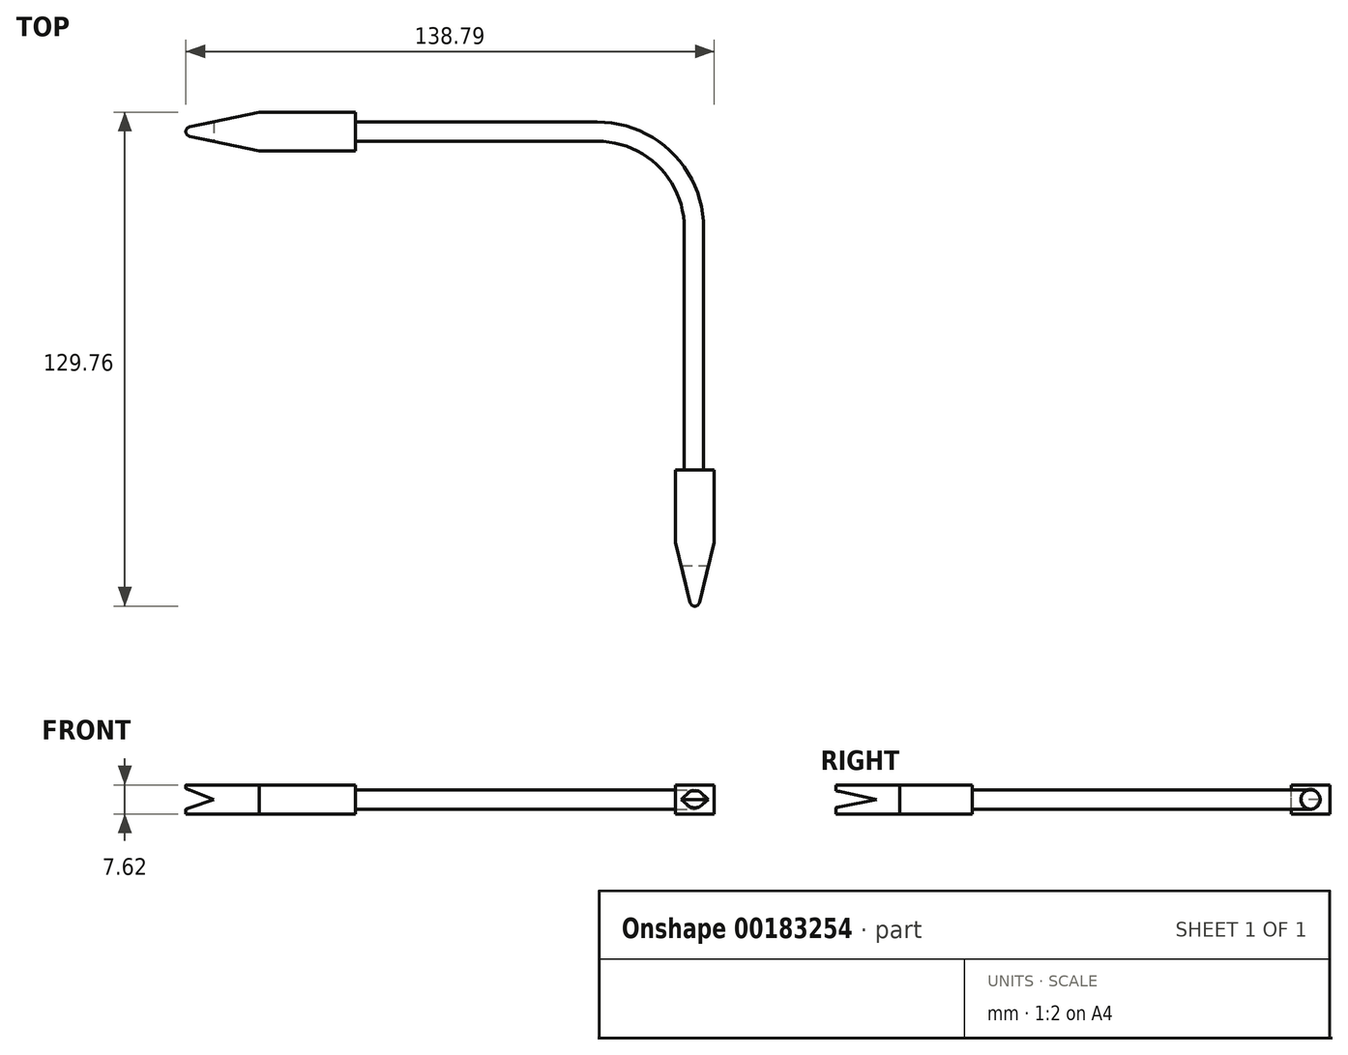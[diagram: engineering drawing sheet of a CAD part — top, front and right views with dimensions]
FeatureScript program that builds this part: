
annotation { "Feature Type Name" : "Feature", "Feature Type Description" : "" }
export const myFeature = defineFeature(function(context is Context, id is Id, definition is map)
    precondition{}
    {
        {
            var Q0;
            Q0=qCreatedBy(makeId("Right.planeOp"),FACE);
            var sketch = newSketch(context, id + "F0", { "sketchPlane" : qUnion([Q0])});
            skCircle(sketch, "E0", {"center": v(0, 0) * mm, "radius": 2.54 * mm});
            skSolve(sketch);
        }
        {
            var Q0;
            Q0=qCreatedBy(makeId("Top.planeOp"),FACE);
            var sketch = newSketch(context, id + "F1", { "sketchPlane" : qUnion([Q0])});
            skLineSegment(sketch, "E1", {"start": v(0, 0) * mm, "end": v(63.5, 0) * mm});
            skLineSegment(sketch, "E2", {"start": v(63.5, 0) * mm, "end": v(63.5, -64.55) * mm, "construction": true});
            skArc(sketch, "E3", {"start": v(88.9, -25.4) * mm, "mid": v(81.46, -7.44) * mm, "end": v(63.5, 0) * mm});
            skLineSegment(sketch, "E4", {"start": v(88.9, -25.4) * mm, "end": v(88.9, -88.9) * mm});
            skSolve(sketch);
        }
        {
            var Q0;
            Q0=makeQuery(id+"F0.imprint","IMPRINT",FACE,{"disambiguationData":[TD([[makeQuery(id+"F0.imprint","IMPRINT",EDGE,{"derivedFrom":sQuery(id+"F0.wireOp",EDGE,"E0")}),1.0]])]});
            var Q1;
            Q1=sQuery(id+"F1.wireOp",EDGE,"E1");
            var Q2;
            Q2=sQuery(id+"F1.wireOp",EDGE,"E3");
            var Q3;
            Q3=sQuery(id+"F1.wireOp",EDGE,"E4");
            sweep(context, id + "F2", {"profiles" : qUnion([Q0]), "path" : qUnion([Q1, Q2, Q3])});
        }
        {
            var Q0;
            Q0=qCreatedBy(makeId("Top.planeOp"),FACE);
            var sketch = newSketch(context, id + "F3", { "sketchPlane" : qUnion([Q0])});
            skLineSegment(sketch, "E5.bottom", {"start": v(0, 5.08) * mm, "end": v(-25.36, 5.08) * mm});
            skLineSegment(sketch, "E5.top", {"start": v(0, -5.08) * mm, "end": v(-25.36, -5.08) * mm});
            skLineSegment(sketch, "E5.left", {"start": v(0, 5.08) * mm, "end": v(0, -5.08) * mm});
            skLineSegment(sketch, "E5.right", {"start": v(-25.36, 5.08) * mm, "end": v(-25.36, -5.08) * mm});
            skSolve(sketch);
        }
        {
            var Q0;
            Q0=makeQuery(id+"F3.imprint","IMPRINT",FACE,{"disambiguationData":[TD([[makeQuery(id+"F3.imprint","IMPRINT",EDGE,{"derivedFrom":sQuery(id+"F3.wireOp",EDGE,"E5.bottom")}),1.0]])]});
            extrude(context, id + "F4", {"entities" : qUnion([Q0]), "operationType" : NewBodyOperationType.ADD, "endBound" : BoundingType.SYMMETRIC, "oppositeDirection" : true, "depth" : 7.62 * mm});
        }
        {
            var Q0;
            Q0=makeQuery(id+"F4.opExtrude","CAP_FACE",FACE,{"disambiguationData":[OSD([sQuery(id+"F3.wireOp",EDGE,"E5.bottom"),sQuery(id+"F3.wireOp",EDGE,"E5.top"),sQuery(id+"F3.wireOp",EDGE,"E5.left"),sQuery(id+"F3.wireOp",EDGE,"E5.right")])],"isStart":true});
            var sketch = newSketch(context, id + "F5", { "sketchPlane" : qUnion([Q0])});
            skLineSegment(sketch, "E6", {"start": v(-25.36, 5.08) * mm, "end": v(-49.47, 0) * mm});
            skLineSegment(sketch, "E7", {"start": v(-49.47, 0) * mm, "end": v(-25.36, -5.08) * mm});
            skLineSegment(sketch, "E8", {"start": v(-25.36, -5.08) * mm, "end": v(-25.36, 5.08) * mm});
            skSolve(sketch);
        }
        {
            var Q0;
            Q0=makeQuery(id+"F5.imprint","IMPRINT",FACE,{"disambiguationData":[TD([[makeQuery(id+"F5.imprint","IMPRINT",EDGE,{"derivedFrom":sQuery(id+"F5.wireOp",EDGE,"E6")}),1.0]])]});
            var Q1;
            Q1=makeQuery(id+"F4.opExtrude","CAP_FACE",FACE,{"disambiguationData":[OSD([sQuery(id+"F3.wireOp",EDGE,"E5.bottom"),sQuery(id+"F3.wireOp",EDGE,"E5.top"),sQuery(id+"F3.wireOp",EDGE,"E5.left"),sQuery(id+"F3.wireOp",EDGE,"E5.right")])],"isStart":false});
            extrude(context, id + "F6", {"entities" : qUnion([Q0]), "operationType" : NewBodyOperationType.ADD, "endBound" : BoundingType.UP_TO_SURFACE, "oppositeDirection" : true, "endBoundEntityFace" : qUnion([Q1]), "depth" : 25.4 * mm});
        }
        {
            var Q0;
            Q0=makeQuery(id+"F6.opExtrude","SWEPT_EDGE",EDGE,{"disambiguationData":[OSD([sQuery(id+"F5.wireOp",EDGE,"E6"),sQuery(id+"F5.wireOp",EDGE,"E7")])]});
            fillet(context, id + "F7", {"entities" : qUnion([Q0]), "radius" : 1.27 * mm, "tangentPropagation" : true, "allowEdgeOverflow" : false});
        }
        {
            var Q0;
            Q0=makeQuery(id+"F4.opExtrude","SWEPT_FACE",FACE,{"disambiguationData":[OSD([sQuery(id+"F3.wireOp",EDGE,"E5.top")])]});
            var sketch = newSketch(context, id + "F8", { "sketchPlane" : qUnion([Q0])});
            skLineSegment(sketch, "E9", {"start": v(-37.22, 0) * mm, "end": v(-46.26, 3.53) * mm});
            skLineSegment(sketch, "E10", {"start": v(-37.22, 0) * mm, "end": v(-46.26, -3.1) * mm});
            skLineSegment(sketch, "E11", {"start": v(-46.26, -3.1) * mm, "end": v(-46.26, 3.53) * mm});
            skSolve(sketch);
        }
        {
            var Q0;
            Q0=makeQuery(id+"F8.imprint","IMPRINT",FACE,{"disambiguationData":[TD([[makeQuery(id+"F8.imprint","IMPRINT",EDGE,{"derivedFrom":sQuery(id+"F8.wireOp",EDGE,"E9")}),1.0]])]});
            extrude(context, id + "F9", {"entities" : qUnion([Q0]), "operationType" : NewBodyOperationType.REMOVE, "oppositeDirection" : true, "depth" : 25.4 * mm});
        }
        {
            var Q0;
            Q0=qCreatedBy(makeId("Top.planeOp"),FACE);
            var sketch = newSketch(context, id + "F10", { "sketchPlane" : qUnion([Q0])});
            skLineSegment(sketch, "E12.bottom", {"start": v(84.05, -88.9) * mm, "end": v(94.2, -88.9) * mm, "construction": true});
            skLineSegment(sketch, "E12.left", {"start": v(84.05, -88.9) * mm, "end": v(84.05, -107.95) * mm, "construction": true});
            skLineSegment(sketch, "E12.right", {"start": v(94.2, -88.9) * mm, "end": v(94.2, -107.95) * mm, "construction": true});
            skLineSegment(sketch, "E13.bottom", {"start": v(84.05, -88.9) * mm, "end": v(94.2, -88.9) * mm});
            skLineSegment(sketch, "E13.left", {"start": v(84.05, -88.9) * mm, "end": v(84.05, -107.95) * mm});
            skLineSegment(sketch, "E13.right", {"start": v(94.2, -88.9) * mm, "end": v(94.2, -107.95) * mm});
            skLineSegment(sketch, "E14", {"start": v(84.05, -107.95) * mm, "end": v(89.13, -128.77) * mm});
            skPoint(sketch, "E14.endSnap0", {"position": v(89.13, -107.95) * mm});
            skLineSegment(sketch, "E15", {"start": v(89.13, -128.77) * mm, "end": v(94.2, -107.95) * mm});
            skSolve(sketch);
        }
        {
            var Q0;
            Q0=makeQuery(id+"F10.imprint","IMPRINT",FACE,{"disambiguationData":[TD([[makeQuery(id+"F10.imprint","IMPRINT",EDGE,{"derivedFrom":sQuery(id+"F10.wireOp",EDGE,"E13.bottom")}),-1.0]])]});
            extrude(context, id + "F11", {"entities" : qUnion([Q0]), "operationType" : NewBodyOperationType.ADD, "endBound" : BoundingType.SYMMETRIC, "oppositeDirection" : true, "depth" : 7.62 * mm});
        }
        {
            var Q0;
            Q0=makeQuery(id+"F11.opExtrude","SWEPT_EDGE",EDGE,{"disambiguationData":[OSD([sQuery(id+"F10.wireOp",EDGE,"E14"),sQuery(id+"F10.wireOp",EDGE,"E15")])]});
            fillet(context, id + "F12", {"entities" : qUnion([Q0]), "radius" : 1.27 * mm, "tangentPropagation" : true, "allowEdgeOverflow" : false});
        }
        {
            var Q0;
            Q0=makeQuery(id+"F11.opExtrude","SWEPT_FACE",FACE,{"disambiguationData":[OSD([sQuery(id+"F10.wireOp",EDGE,"E13.right")])]});
            var sketch = newSketch(context, id + "F13", { "sketchPlane" : qUnion([Q0])});
            skLineSegment(sketch, "E16", {"start": v(-114.07, 0) * mm, "end": v(-128.7, 3.18) * mm});
            skLineSegment(sketch, "E17", {"start": v(-114.07, 0) * mm, "end": v(-128.7, -2.94) * mm});
            skLineSegment(sketch, "E18", {"start": v(-128.7, -2.94) * mm, "end": v(-128.7, 3.18) * mm});
            skSolve(sketch);
        }
        {
            var Q0;
            Q0=makeQuery(id+"F13.imprint","IMPRINT",FACE,{"disambiguationData":[TD([[makeQuery(id+"F13.imprint","IMPRINT",EDGE,{"derivedFrom":sQuery(id+"F13.wireOp",EDGE,"E16")}),1.0]])]});
            extrude(context, id + "F14", {"entities" : qUnion([Q0]), "operationType" : NewBodyOperationType.REMOVE, "oppositeDirection" : true, "depth" : 25.4 * mm});
        }
    });
